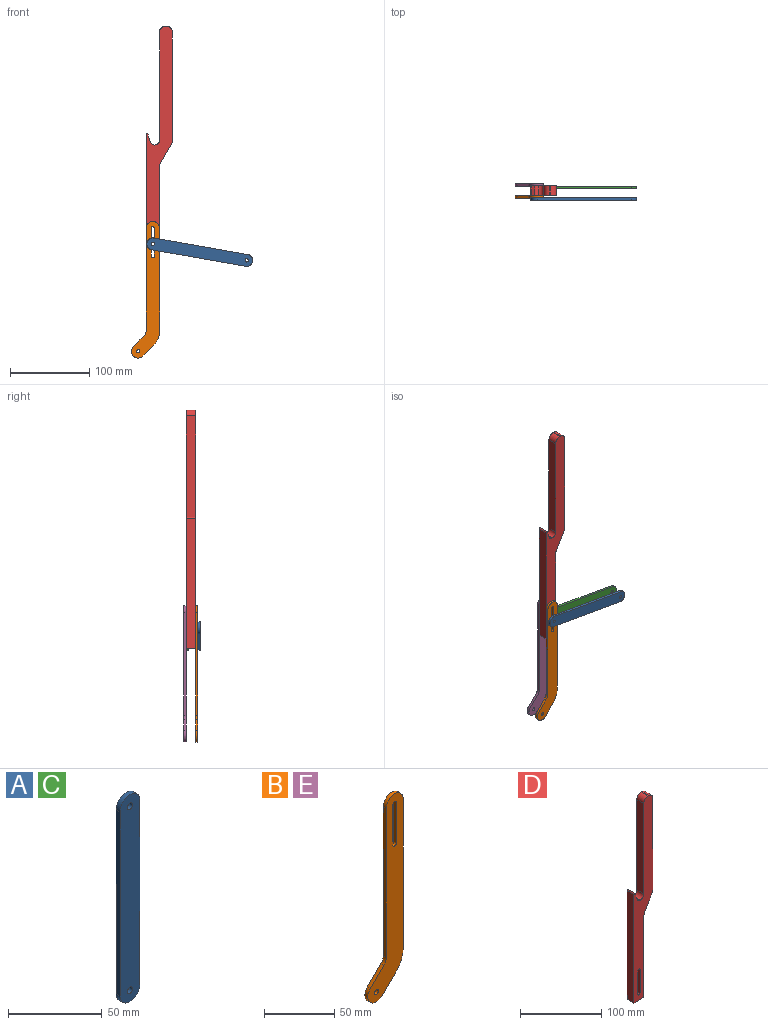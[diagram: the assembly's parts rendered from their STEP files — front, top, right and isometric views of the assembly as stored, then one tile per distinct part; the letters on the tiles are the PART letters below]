
ASSEMBLY  parts=5 mates=7
PART A: 8 faces, bbox 15x3x135 mm
  f0: plane 120x3mm, normal (-1,0,0), area 360mm2, adj f1,f4,f6,f7
  f1: cylinder r=7.5mm len=15mm, axis (0,1,0), area 70.7mm2, adj f0,f2,f6,f7
  f2: plane 120x3mm, normal (1,0,0), area 360mm2, adj f1,f4,f6,f7
  f3: cylinder r=2mm len=4mm, axis (0,1,0), area 37.7mm2, adj f6,f7
  f4: cylinder r=7.5mm len=15mm, axis (0,1,0), area 70.7mm2, adj f0,f2,f6,f7
  f5: cylinder r=2mm len=4mm, axis (0,1,0), area 37.7mm2, adj f6,f7
  f6: plane 135x15mm, normal (0,-1,0), area 1951.6mm2, adj f0,f1,f2,f3,f4,f5
  f7: plane 135x15mm, normal (0,1,0), area 1951.6mm2, adj f0,f1,f2,f3,f4,f5
PART B: 15 faces, bbox 35.5x3x172 mm
  f0: plane 35x3mm, normal (1,0,0), area 105mm2, adj f1,f12,f13,f14
  f1: cylinder r=2mm len=4mm, axis (0,1,0), area 18.8mm2, adj f0,f2,f13,f14
  f2: plane 35x3mm, normal (-1,0,0), area 105mm2, adj f1,f12,f13,f14
  f3: plane 129.67x3mm, normal (1,0,0), area 389mm2, adj f4,f10,f13,f14
  f4: cylinder r=8.5mm len=17mm, axis (0,1,0), area 80.1mm2, adj f3,f5,f13,f14
  f5: plane 129.67x3mm, normal (-1,0,0), area 389mm2, adj f4,f6,f13,f14
  f6: cylinder r=8mm len=5.66mm, axis (0,1,0), area 18.8mm2, adj f5,f7,f13,f14
  f7: plane 13.67x13.67mm, normal (-0.71,0,0.71), area 58mm2, adj f6,f8,f13,f14
  f8: cylinder r=8.5mm len=14.51mm, axis (0,1,0), area 80.1mm2, adj f7,f9,f13,f14
  f9: plane 13.67x13.67mm, normal (0.71,0,-0.71), area 58mm2, adj f8,f10,f13,f14
  f10: cylinder r=25mm len=17.68mm, axis (0,1,0), area 58.9mm2, adj f3,f9,f13,f14
  f11: cylinder r=2mm len=4mm, axis (0,1,0), area 37.7mm2, adj f13,f14
  f12: cylinder r=2mm len=4mm, axis (0,1,0), area 18.8mm2, adj f0,f2,f13,f14
  f13: plane 172x35.5mm, normal (0,-1,0), area 2815mm2, adj f0,f1,f2,f3,f4,f5,f6,f7
  f14: plane 172x35.5mm, normal (0,1,0), area 2815mm2, adj f0,f1,f2,f3,f4,f5,f6,f7
PART C: same geometry as A
PART D: 23 faces, bbox 33x12x300 mm
  f0: plane 35x12mm, normal (1,0,0), area 420mm2, adj f1,f20,f21,f22
  f1: cylinder r=2mm len=12mm, axis (0,1,0), area 75.4mm2, adj f0,f2,f21,f22
  f2: plane 35x12mm, normal (-1,0,0), area 420mm2, adj f1,f20,f21,f22
  f3: cylinder r=6mm len=12mm, axis (0,1,0), area 113.1mm2, adj f4,f19,f21,f22
  f4: plane 12x0.5mm, normal (0,0,1), area 6mm2, adj f3,f5,f21,f22
  f5: cylinder r=5mm len=12mm, axis (0,1,0), area 73.3mm2, adj f4,f6,f21,f22
  f6: plane 12x10.72mm, normal (0.94,0,0.34), area 136.9mm2, adj f5,f7,f21,f22
  f7: cylinder r=1.5mm len=12mm, axis (0,1,0), area 15.8mm2, adj f6,f8,f21,f22
  f8: cylinder r=1.5mm len=12mm, axis (0,1,0), area 22.1mm2, adj f7,f9,f21,f22
  f9: plane 163.5x12mm, normal (-1,0,0), area 1962mm2, adj f8,f10,f21,f22
  f10: plane 17x12mm, normal (0,0,-1), area 204mm2, adj f9,f11,f21,f22
  f11: plane 122.32x12mm, normal (1,0,0), area 1467.8mm2, adj f10,f12,f21,f22
  f12: cylinder r=10mm len=12mm, axis (0,1,0), area 62.8mm2, adj f11,f13,f21,f22
  f13: plane 23.07x13.32mm, normal (0.87,0,-0.5), area 319.7mm2, adj f12,f14,f21,f22
  f14: cylinder r=10mm len=12mm, axis (0,1,0), area 62.8mm2, adj f13,f15,f21,f22
  f15: plane 137.11x12mm, normal (1,0,0), area 1645.3mm2, adj f14,f16,f21,f22
  f16: cylinder r=7.5mm len=12mm, axis (0,1,0), area 141.4mm2, adj f15,f17,f21,f22
  f17: plane 12x1mm, normal (0,0,1), area 12mm2, adj f16,f18,f21,f22
  f18: cylinder r=7.5mm len=12mm, axis (0,1,0), area 141.4mm2, adj f17,f19,f21,f22
  f19: plane 136.5x12mm, normal (-1,0,0), area 1638mm2, adj f3,f18,f21,f22
  f20: cylinder r=2mm len=12mm, axis (0,1,0), area 75.4mm2, adj f0,f2,f21,f22
  f21: plane 300x33mm, normal (0,-1,0), area 5024.9mm2, adj f0,f1,f2,f3,f4,f5,f6,f7
  f22: plane 300x33mm, normal (0,1,0), area 5024.9mm2, adj f0,f1,f2,f3,f4,f5,f6,f7
PART E: same geometry as B
PLACE A rot(axis=(0,1,0),100deg) t=(136.91,-3,190.22)mm
PLACE B at identity
PLACE C rot(axis=(0,1,0),100deg) t=(136.91,12,190.22)mm
PLACE D at identity fixed
PLACE E t=(0,15,0)mm
MATE cylindrical D.f1 <-> B.f1  axis (0,-1,0) through (158.61,-12,45)mm
MATE cylindrical D.f20 <-> E.f12  axis (0,1,0) through (158.61,0,10)mm
MATE cylindrical C.f1 <-> A.f1  axis (0,1,0) through (158.61,0,25.34)mm
MATE cylindrical D.f1 <-> E.f1  axis (0,1,0) through (158.61,0,45)mm
MATE cylindrical A.f3 <-> C.f3  axis (0,-1,0) through (276.78,-18,4.5)mm
MATE planar B.f1 <-> A.f1  axis (0,-1,0) through (158.61,-15,45)mm
MATE cylindrical D.f20 <-> B.f12  axis (0,1,0) through (158.61,-12,10)mm
